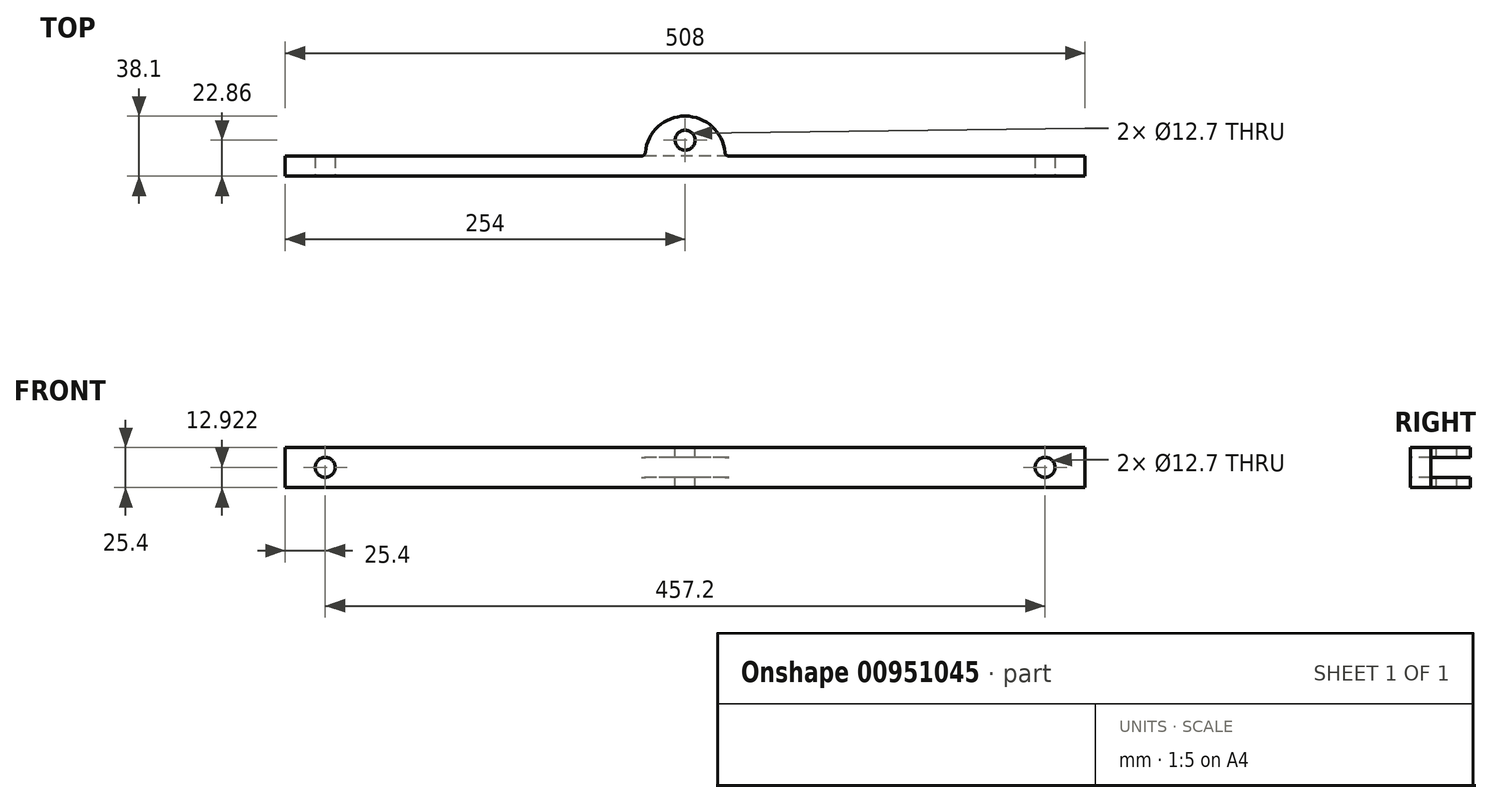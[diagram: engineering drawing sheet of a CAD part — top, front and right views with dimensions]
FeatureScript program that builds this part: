
annotation { "Feature Type Name" : "Feature", "Feature Type Description" : "" }
export const myFeature = defineFeature(function(context is Context, id is Id, definition is map)
    precondition{}
    {
        {
            var Q0;
            Q0=qCreatedBy(makeId("Top.planeOp"),FACE);
            var sketch = newSketch(context, id + "F0", { "sketchPlane" : qUnion([Q0])});
            skLineSegment(sketch, "E0.bottom", {"start": v(254, -6.35) * mm, "end": v(-254, -6.35) * mm});
            skLineSegment(sketch, "E0.top", {"start": v(254, 6.35) * mm, "end": v(-254, 6.35) * mm});
            skLineSegment(sketch, "E0.left", {"start": v(254, -6.35) * mm, "end": v(254, 6.35) * mm});
            skLineSegment(sketch, "E0.right", {"start": v(-254, -6.35) * mm, "end": v(-254, 6.35) * mm});
            skPoint(sketch, "E0.middle", {"position": v(0, 0) * mm});
            skArc(sketch, "E1", {"start": v(25.4, 6.35) * mm, "mid": v(0, 31.75) * mm, "end": v(-25.4, 6.35) * mm});
            skSolve(sketch);
        }
        {
            var Q0;
            Q0 = qSketchRegion(id + "F0", true);
            extrude(context, id + "F1", {"entities" : qUnion([Q0]), "depth" : 25.4 * mm, "offsetDistance" : 25.4 * mm});
        }
        {
            var Q0;
            Q0=makeQuery(id+"F1.opExtrude","CAP_FACE",FACE,{"disambiguationData":[OSD([sQuery(id+"F0.wireOp",EDGE,"E0.bottom"),sQuery(id+"F0.wireOp",EDGE,"E0.top"),sQuery(id+"F0.wireOp",EDGE,"E0.left"),sQuery(id+"F0.wireOp",EDGE,"E0.right"),sQuery(id+"F0.wireOp",EDGE,"E1")])],"isStart":false});
            var sketch = newSketch(context, id + "F2", { "sketchPlane" : qUnion([Q0])});
            skCircle(sketch, "E2", {"center": v(0, 16.51) * mm, "radius": 6.35 * mm});
            skSolve(sketch);
        }
        {
            var Q0;
            Q0 = qSketchRegion(id + "F2", true);
            extrude(context, id + "F3", {"entities" : qUnion([Q0]), "operationType" : NewBodyOperationType.REMOVE, "endBound" : BoundingType.THROUGH_ALL, "oppositeDirection" : true, "depth" : 25.4 * mm, "offsetDistance" : 25.4 * mm});
        }
        {
            var Q0;
            Q0=makeQuery(id+"F1.opExtrude","SWEPT_FACE",FACE,{"disambiguationData":[OSD([sQuery(id+"F0.wireOp",EDGE,"E0.right")])]});
            var sketch = newSketch(context, id + "F4", { "sketchPlane" : qUnion([Q0])});
            skLineSegment(sketch, "E3", {"start": v(-6.35, 0) * mm, "end": v(-6.35, 25.4) * mm, "construction": true});
            skLineSegment(sketch, "E4", {"start": v(-6.35, 12.7) * mm, "end": v(6.35, 12.7) * mm, "construction": true});
            skLineSegment(sketch, "E5.bottom", {"start": v(-6.35, 19.05) * mm, "end": v(-48.08, 19.05) * mm});
            skLineSegment(sketch, "E5.top", {"start": v(-6.35, 6.35) * mm, "end": v(-48.08, 6.35) * mm});
            skLineSegment(sketch, "E5.left", {"start": v(-6.35, 19.05) * mm, "end": v(-6.35, 6.35) * mm});
            skLineSegment(sketch, "E5.right", {"start": v(-48.08, 19.05) * mm, "end": v(-48.08, 6.35) * mm});
            skPoint(sketch, "E5.middle", {"position": v(-27.22, 12.7) * mm});
            skSolve(sketch);
        }
        {
            var Q0;
            Q0 = qSketchRegion(id + "F4", true);
            extrude(context, id + "F5", {"entities" : qUnion([Q0]), "operationType" : NewBodyOperationType.REMOVE, "endBound" : BoundingType.THROUGH_ALL, "oppositeDirection" : true, "depth" : 25.4 * mm, "offsetDistance" : 25.4 * mm});
        }
        {
            var Q0;
            {var subQ0=sQuery(id+"F0.wireOp",EDGE,"E1");var subQ2=sQuery(id+"F0.wireOp",EDGE,"E0.top");var subQ3=makeQuery(id+"F0.imprint","INTERSECT",VERTEX,{"disambiguationData":[OD(1.0)],"derivedFrom":[subQ2,subQ0]});Q0=makeQuery(id+"F5.boolean.opBoolean","SPLIT",EDGE,{"disambiguationData":[TD([makeQuery(id+"F5.opExtrude","SWEPT_FACE",FACE,{"disambiguationData":[OSD([sQuery(id+"F4.wireOp",EDGE,"E5.top")])]})])],"derivedFrom":makeQuery(id+"F1.opExtrude","SWEPT_EDGE",EDGE,{"disambiguationData":[OSD([subQ2,subQ0]),TDD([subQ3])]})});}
            var Q1;
            {var subQ1=sQuery(id+"F0.wireOp",EDGE,"E0.top");var subQ2=sQuery(id+"F0.wireOp",EDGE,"E1");var subQ3=makeQuery(id+"F0.imprint","INTERSECT",VERTEX,{"disambiguationData":[OD(1.0)],"derivedFrom":[subQ1,subQ2]});Q1=makeQuery(id+"F5.boolean.opBoolean","SPLIT",EDGE,{"disambiguationData":[TD([makeQuery(id+"F5.opExtrude","SWEPT_FACE",FACE,{"disambiguationData":[OSD([sQuery(id+"F4.wireOp",EDGE,"E5.bottom")])]})])],"derivedFrom":makeQuery(id+"F1.opExtrude","SWEPT_EDGE",EDGE,{"disambiguationData":[OSD([subQ1,subQ2]),TDD([subQ3])]})});}
            var Q2;
            {var subQ1=sQuery(id+"F0.wireOp",EDGE,"E0.top");var subQ2=sQuery(id+"F0.wireOp",EDGE,"E1");var subQ4=makeQuery(id+"F0.imprint","INTERSECT",VERTEX,{"disambiguationData":[OD(0.0)],"derivedFrom":[subQ1,subQ2]});Q2=makeQuery(id+"F5.boolean.opBoolean","SPLIT",EDGE,{"disambiguationData":[TD([makeQuery(id+"F5.opExtrude","SWEPT_FACE",FACE,{"disambiguationData":[OSD([sQuery(id+"F4.wireOp",EDGE,"E5.bottom")])]})])],"derivedFrom":makeQuery(id+"F1.opExtrude","SWEPT_EDGE",EDGE,{"disambiguationData":[OSD([subQ1,subQ2]),TDD([subQ4])]})});}
            var Q3;
            {var subQ0=sQuery(id+"F0.wireOp",EDGE,"E1");var subQ2=sQuery(id+"F0.wireOp",EDGE,"E0.top");var subQ4=makeQuery(id+"F0.imprint","INTERSECT",VERTEX,{"disambiguationData":[OD(0.0)],"derivedFrom":[subQ2,subQ0]});Q3=makeQuery(id+"F5.boolean.opBoolean","SPLIT",EDGE,{"disambiguationData":[TD([makeQuery(id+"F5.opExtrude","SWEPT_FACE",FACE,{"disambiguationData":[OSD([sQuery(id+"F4.wireOp",EDGE,"E5.top")])]})])],"derivedFrom":makeQuery(id+"F1.opExtrude","SWEPT_EDGE",EDGE,{"disambiguationData":[OSD([subQ2,subQ0]),TDD([subQ4])]})});}
            fillet(context, id + "F6", {"entities" : qUnion([Q0, Q1, Q2, Q3]), "radius" : 2.54 * mm, "tangentPropagation" : true, "allowEdgeOverflow" : false});
        }
        {
            var Q0;
            Q0=makeQuery(id+"F1.opExtrude","SWEPT_FACE",FACE,{"disambiguationData":[OSD([sQuery(id+"F0.wireOp",EDGE,"E0.bottom")])]});
            var sketch = newSketch(context, id + "F7", { "sketchPlane" : qUnion([Q0])});
            skLineSegment(sketch, "E6", {"start": v(0, 0) * mm, "end": v(0, 25.4) * mm, "construction": true});
            skCircle(sketch, "E7", {"center": v(-228.6, 12.92) * mm, "radius": 6.35 * mm});
            skCircle(sketch, "E8", {"center": v(228.6, 12.92) * mm, "radius": 6.35 * mm});
            skLineSegment(sketch, "E9", {"start": v(-228.6, 12.92) * mm, "end": v(0, 12.92) * mm, "construction": true});
            skLineSegment(sketch, "E10", {"start": v(0, 12.92) * mm, "end": v(228.6, 12.92) * mm, "construction": true});
            skSolve(sketch);
        }
        {
            var Q0;
            Q0 = qSketchRegion(id + "F7", true);
            extrude(context, id + "F8", {"entities" : qUnion([Q0]), "operationType" : NewBodyOperationType.REMOVE, "endBound" : BoundingType.THROUGH_ALL, "oppositeDirection" : true, "depth" : 25.4 * mm, "offsetDistance" : 25.4 * mm});
        }
    });
